# Revit family: Specialty_Equipment-Bavis_Fabacraft-Captive_Carrier_TransTrax-Reverse
name_source: partatom
category: Specialty Equipment
units: mm (PartAtom-declared; Revit-internal decimal feet)

## family parameters
Always vertical = Yes
Cut with Voids When Loaded = No
Host = Wall
OmniClass Number = 23.50.30.24
OmniClass Title = Conveyors
Part Type = Normal
Room Calculation Point = No
Round Connector Dimension = Use Diameter
Shared = No

## types (1)
- Reverse
    Apparent Load = 0 VA
    Assembly Code = E1010
    C Left Side Carrier = No
    C Right Side Carrier = Yes
    Car Finish = Paint - Bavis Fabacraft - Red
    Default Elevation = 0' - 0"
    Description = High-Capacity Carrier; Standard Track
    Instruction Sheet Link = https://docs.bavis.com
    Keynote = 14 90 00
    Load Classification = Power
    Manufacturer = Bavis Fabacraft
    Model = See Order Code
    Number of Poles = 1
    Power Factor = 1
    Product Documentation Link = https://docs.bavis.com
    Product Name = Captive Carrier TransTrax Remote Lane Delivery System - Reverse
    Product Page URL = https://www.bavis.com
    Track Finish = Metal - Bavis Fabacraft - Aluminum
    Trim Finish = Metal - Bavis Fabacraft - Aluminum
    Twist Finish = Metal - Bavis Fabacraft - Steel
    URL = https://www.bavis.com
    Version = 2020 - v1.0a
    Video Link = https://www.youtube.com
    Voltage = 120 V

## geometry (parser evidence)
native form markers: Sweep x12
no freeform markers — native parametric forms only
